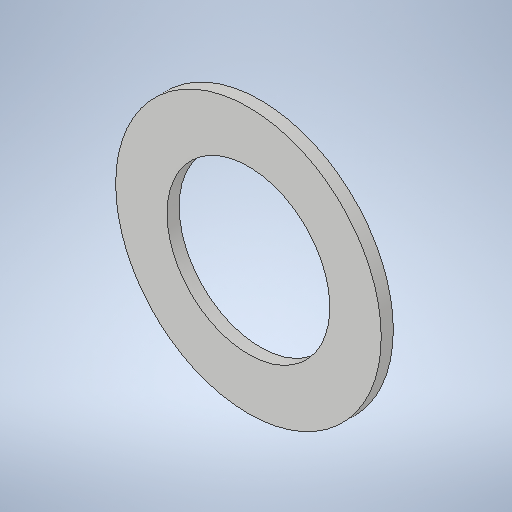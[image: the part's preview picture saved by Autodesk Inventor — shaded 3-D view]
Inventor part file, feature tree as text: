
AUTODESK INVENTOR PART (.ipt)
format: ipt  version: 2025 (Build 290162000, 162)  size: 1,304,576 bytes
history: native  units: mm
features: extrude x2
ambient origin geometry x8: Origin, YZ Plane, XZ Plane, XY Plane, X Axis, Y Axis, Z Axis, Center Point
bodies: Volumenkörper1 (feature_tree)
feature tree (2):
  extrude  "Extrusion1"  Depth=53.88mm
  extrude  "Extrusion2"  Depth=87.9mm
